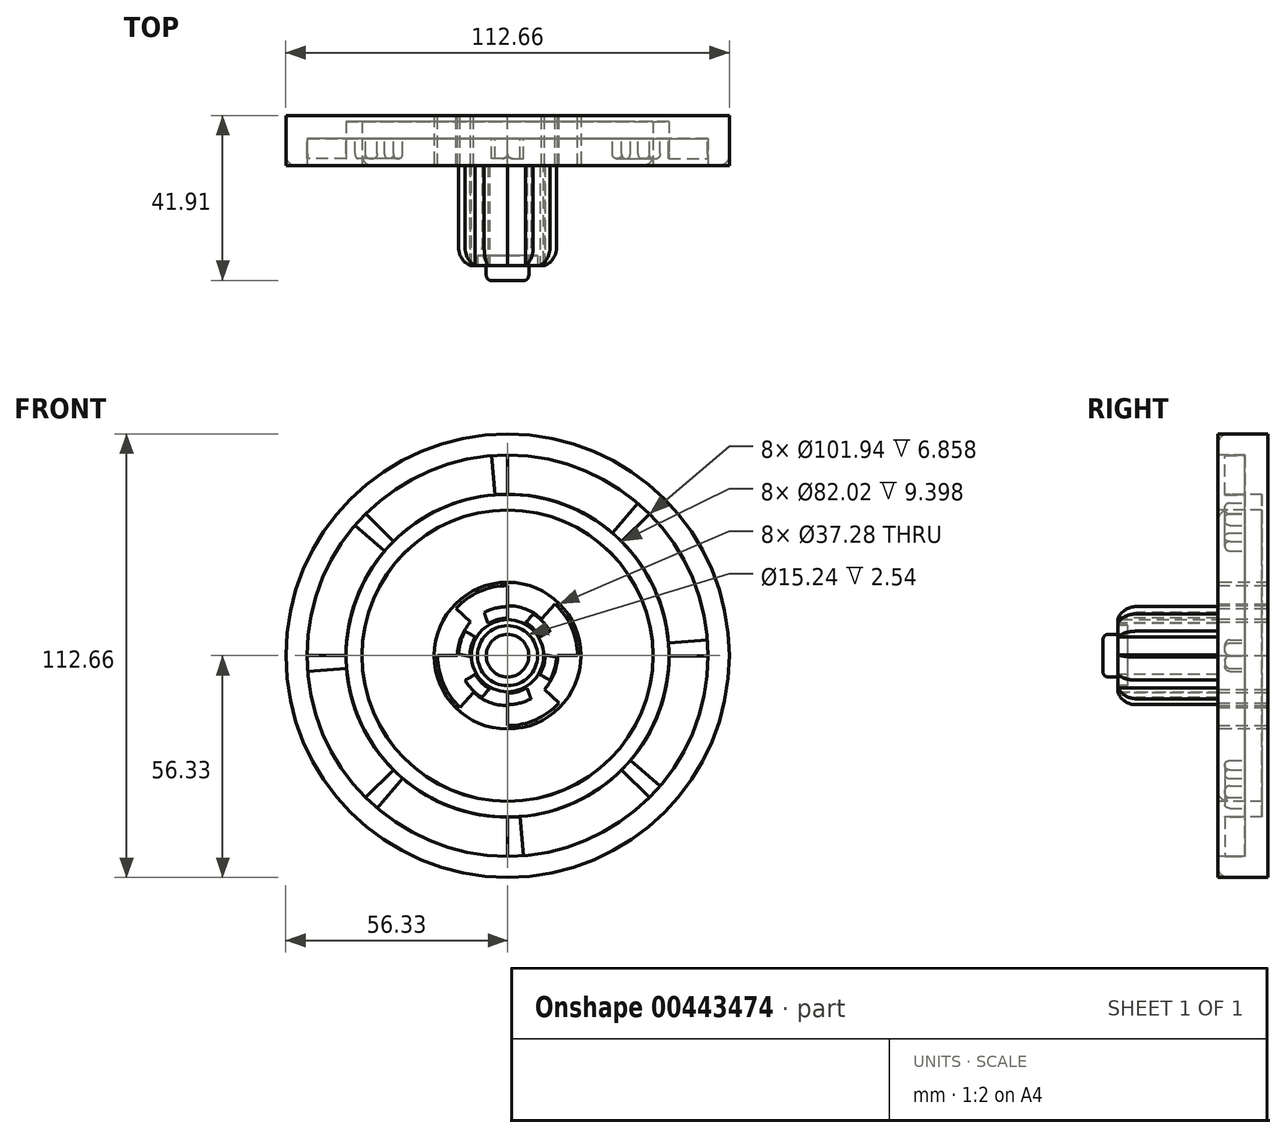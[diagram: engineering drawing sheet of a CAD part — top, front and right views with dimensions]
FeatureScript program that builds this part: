
annotation { "Feature Type Name" : "Feature", "Feature Type Description" : "" }
export const myFeature = defineFeature(function(context is Context, id is Id, definition is map)
    precondition{}
    {
        {
            var Q0;
            Q0=qCreatedBy(makeId("Front.planeOp"),FACE);
            var sketch = newSketch(context, id + "F0", { "sketchPlane" : qUnion([Q0])});
            skCircle(sketch, "E0", {"center": v(0, 0) * mm, "radius": 56.33 * mm});
            skSolve(sketch);
        }
        {
            var Q0;
            Q0=makeQuery(id+"F0.imprint","IMPRINT",FACE,{"disambiguationData":[TD([[makeQuery(id+"F0.imprint","IMPRINT",EDGE,{"derivedFrom":sQuery(id+"F0.wireOp",EDGE,"E0")}),1.0]])]});
            extrude(context, id + "F1", {"entities" : qUnion([Q0]), "depth" : 12.7 * mm});
        }
        {
            var Q0;
            Q0=makeQuery(id+"F1.opExtrude","CAP_FACE",FACE,{"disambiguationData":[OSD([sQuery(id+"F0.wireOp",EDGE,"E0")])],"isStart":false});
            var sketch = newSketch(context, id + "F2", { "sketchPlane" : qUnion([Q0])});
            skCircle(sketch, "E1", {"center": v(0, 0) * mm, "radius": 36.97 * mm});
            skCircle(sketch, "E2", {"center": v(0, 0) * mm, "radius": 50.97 * mm});
            skSolve(sketch);
        }
        {
            var Q0;
            Q0=makeQuery(id+"F2.imprint","IMPRINT",FACE,{"disambiguationData":[TD([[makeQuery(id+"F2.imprint","IMPRINT",EDGE,{"derivedFrom":sQuery(id+"F2.wireOp",EDGE,"E1")}),-1.0]])]});
            extrude(context, id + "F3", {"entities" : qUnion([Q0]), "operationType" : NewBodyOperationType.REMOVE, "oppositeDirection" : true, "depth" : 6.86 * mm});
        }
        {
            var Q0;
            Q0=makeQuery(id+"F3.boolean.opBoolean","COPY",FACE,{"derivedFrom":makeQuery(id+"F3.opExtrude","CAP_FACE",FACE,{"disambiguationData":[OSD([sQuery(id+"F2.wireOp",EDGE,"E1"),sQuery(id+"F2.wireOp",EDGE,"E2")])],"isStart":false})});
            var sketch = newSketch(context, id + "F4", { "sketchPlane" : qUnion([Q0])});
            skCircle(sketch, "E3", {"center": v(0, 0) * mm, "radius": 36.99 * mm});
            skCircle(sketch, "E4", {"center": v(0, 0) * mm, "radius": 41 * mm});
            skSolve(sketch);
        }
        {
            var Q0;
            Q0=makeQuery(id+"F4.imprint","IMPRINT",FACE,{"disambiguationData":[TD([[makeQuery(id+"F4.imprint","IMPRINT",EDGE,{"derivedFrom":sQuery(id+"F4.wireOp",EDGE,"E3")}),-1.0]])]});
            extrude(context, id + "F5", {"entities" : qUnion([Q0]), "operationType" : NewBodyOperationType.REMOVE, "oppositeDirection" : true, "depth" : 4.32 * mm});
        }
        {
            var Q0;
            {var subQ0=sQuery(id+"F2.wireOp",EDGE,"E2");Q0=makeQuery(id+"F5.boolean.opBoolean","SPLIT",FACE,{"disambiguationData":[TD([makeQuery(id+"F3.boolean.opBoolean","COPY",FACE,{"derivedFrom":makeQuery(id+"F3.opExtrude","SWEPT_FACE",FACE,{"disambiguationData":[OSD([subQ0])]})})])],"derivedFrom":makeQuery(id+"F3.boolean.opBoolean","COPY",FACE,{"derivedFrom":makeQuery(id+"F3.opExtrude","CAP_FACE",FACE,{"disambiguationData":[OSD([sQuery(id+"F2.wireOp",EDGE,"E1"),subQ0])],"isStart":false})})});}
            var sketch = newSketch(context, id + "F6", { "sketchPlane" : qUnion([Q0])});
            skLineSegment(sketch, "E5", {"start": v(0, 0) * mm, "end": v(33.1, 38.77) * mm});
            skLineSegment(sketch, "E6", {"start": v(0, 0) * mm, "end": v(36.07, 36.02) * mm});
            skSolve(sketch);
        }
        {
            var Q0;
            {var subQ0=sQuery(id+"F6.wireOp",EDGE,"E5");var subQ1=makeQuery(id+"F3.boolean.opBoolean","COPY",EDGE,{"derivedFrom":makeQuery(id+"F3.opExtrude","CAP_EDGE",EDGE,{"disambiguationData":[OSD([sQuery(id+"F2.wireOp",EDGE,"E2")])],"isStart":false})});var subQ2=makeQuery(id+"F6.imprint","INTERSECT",VERTEX,{"derivedFrom":[subQ1,subQ0]});Q0=makeQuery(id+"F6.imprint","IMPRINT",FACE,{"disambiguationData":[TD([[makeQuery(id+"F6.imprint","IMPRINT",EDGE,{"disambiguationData":[TD([[subQ2,1.0]])],"derivedFrom":subQ0}),-1.0]])]});}
            extrude(context, id + "F7", {"entities" : qUnion([Q0]), "operationType" : NewBodyOperationType.ADD, "depth" : 5.08 * mm});
        }
        {
            var Q0;
            Q0=makeQuery(id+"F7.opExtrude","CAP_EDGE",EDGE,{"disambiguationData":[OSD([sQuery(id+"F6.wireOp",EDGE,"E6")])],"isStart":false});
            fillet(context, id + "F8", {"entities" : qUnion([Q0]), "radius" : 1.27 * mm, "tangentPropagation" : true, "allowEdgeOverflow" : false});
        }
        {
            var Q0;
            Q0=makeQuery(id+"F1.opExtrude","SWEPT_BODY",BODY,{"disambiguationData":[OSD([sQuery(id+"F0.wireOp",EDGE,"E0")])]});
            var Q1;
            Q1=makeQuery(id+"F3.boolean.opBoolean","COPY",EDGE,{"derivedFrom":makeQuery(id+"F3.opExtrude","CAP_EDGE",EDGE,{"disambiguationData":[OSD([sQuery(id+"F2.wireOp",EDGE,"E1")])],"isStart":true})});
            circularPattern(context, id + "F9", {"entities" : qUnion([Q0]), "axis" : qUnion([Q1]), "angle" : 360 * degree, "instanceCount" : 8, "equalSpace" : true});
        }
        {
            var Q0;
            Q0=makeQuery(id+"F3.boolean.opBoolean","COPY",EDGE,{"derivedFrom":makeQuery(id+"F3.opExtrude","CAP_EDGE",EDGE,{"disambiguationData":[OSD([sQuery(id+"F2.wireOp",EDGE,"E1")])],"isStart":true})});
            fillet(context, id + "F10", {"entities" : qUnion([Q0]), "radius" : 2.54 * mm, "tangentPropagation" : true, "allowEdgeOverflow" : false});
        }
        {
            var Q0;
            Q0=makeQuery(id+"F3.boolean.opBoolean","COPY",EDGE,{"derivedFrom":makeQuery(id+"F3.opExtrude","CAP_EDGE",EDGE,{"disambiguationData":[OSD([sQuery(id+"F2.wireOp",EDGE,"E2")])],"isStart":true})});
            var Q1;
            Q1=makeQuery(id+"F1.opExtrude","CAP_EDGE",EDGE,{"disambiguationData":[OSD([sQuery(id+"F0.wireOp",EDGE,"E0")])],"isStart":false});
            var Q2;
            Q2=makeQuery(id+"F5.boolean.opBoolean","COPY",EDGE,{"derivedFrom":makeQuery(id+"F5.opExtrude","CAP_EDGE",EDGE,{"disambiguationData":[OSD([sQuery(id+"F4.wireOp",EDGE,"E4")])],"isStart":true})});
            fillet(context, id + "F11", {"entities" : qUnion([Q0, Q1, Q2]), "radius" : 2.54 * mm, "tangentPropagation" : true, "allowEdgeOverflow" : false});
        }
        {
            var Q0;
            Q0=makeQuery(id+"F9.opPattern","COPY",FACE,{"derivedFrom":makeQuery(id+"F3.boolean.opBoolean","SPLIT",FACE,{"disambiguationData":[TD([makeQuery(id+"F3.opExtrude","SWEPT_FACE",FACE,{"disambiguationData":[OSD([sQuery(id+"F2.wireOp",EDGE,"E1")])]})])],"derivedFrom":makeQuery(id+"F1.opExtrude","CAP_FACE",FACE,{"disambiguationData":[OSD([sQuery(id+"F0.wireOp",EDGE,"E0")])],"isStart":false})}),"instanceName":"5"});
            var sketch = newSketch(context, id + "F12", { "sketchPlane" : qUnion([Q0])});
            skCircle(sketch, "E7", {"center": v(0, 0) * mm, "radius": 18.64 * mm});
            skSolve(sketch);
        }
        {
            var Q0;
            Q0=makeQuery(id+"F12.imprint","IMPRINT",FACE,{"disambiguationData":[TD([[makeQuery(id+"F12.imprint","IMPRINT",EDGE,{"derivedFrom":sQuery(id+"F12.wireOp",EDGE,"E7")}),1.0]])]});
            extrude(context, id + "F13", {"entities" : qUnion([Q0]), "operationType" : NewBodyOperationType.REMOVE, "oppositeDirection" : true, "depth" : 25.4 * mm});
        }
        {
            var Q0;
            Q0=qCreatedBy(makeId("Front.planeOp"),FACE);
            var sketch = newSketch(context, id + "F14", { "sketchPlane" : qUnion([Q0])});
            skCircle(sketch, "E8", {"center": v(0, 0) * mm, "radius": 12.7 * mm});
            skCircle(sketch, "E9", {"center": v(0, 0) * mm, "radius": 17.78 * mm});
            skLineSegment(sketch, "E10", {"start": v(0, 0) * mm, "end": v(0, 17.78) * mm});
            skLineSegment(sketch, "E11", {"start": v(0, 0) * mm, "end": v(12, 13.12) * mm});
            skLineSegment(sketch, "E12", {"start": v(0, 0) * mm, "end": v(17.78, 0) * mm});
            skLineSegment(sketch, "E13", {"start": v(0, 0) * mm, "end": v(13.12, -12) * mm});
            skLineSegment(sketch, "E14", {"start": v(0, 0) * mm, "end": v(0, -17.78) * mm});
            skLineSegment(sketch, "E15", {"start": v(0, 0) * mm, "end": v(-12, -13.12) * mm});
            skLineSegment(sketch, "E16", {"start": v(0, 0) * mm, "end": v(-17.78, 0) * mm});
            skLineSegment(sketch, "E17", {"start": v(0, 0) * mm, "end": v(-13.12, 12) * mm});
            skSolve(sketch);
        }
        {
            var Q0;
            Q0=makeQuery(id+"F14.imprint","IMPRINT",FACE,{"disambiguationData":[TD([[makeQuery(id+"F14.imprint","IMPRINT",EDGE,{"derivedFrom":sQuery(id+"F14.wireOp",EDGE,"E8")}),1.0]])]});
            var Q1;
            {var subQ0=sQuery(id+"F14.wireOp",EDGE,"E11");var subQ1=sQuery(id+"F14.wireOp",EDGE,"E8");var subQ2=makeQuery(id+"F14.imprint","INTERSECT",VERTEX,{"derivedFrom":[subQ1,subQ0]});Q1=makeQuery(id+"F14.imprint","IMPRINT",FACE,{"disambiguationData":[TD([[makeQuery(id+"F14.imprint","IMPRINT",EDGE,{"disambiguationData":[TD([[subQ2,1.0]])],"derivedFrom":subQ1}),-1.0]])]});}
            var Q2;
            {var subQ0=sQuery(id+"F14.wireOp",EDGE,"E14");var subQ1=sQuery(id+"F14.wireOp",EDGE,"E8");var subQ2=makeQuery(id+"F14.imprint","INTERSECT",VERTEX,{"derivedFrom":[subQ1,subQ0]});Q2=makeQuery(id+"F14.imprint","IMPRINT",FACE,{"disambiguationData":[TD([[makeQuery(id+"F14.imprint","IMPRINT",EDGE,{"disambiguationData":[TD([[subQ2,-1.0]])],"derivedFrom":subQ1}),-1.0]])]});}
            var Q3;
            {var subQ0=sQuery(id+"F14.wireOp",EDGE,"E16");var subQ1=sQuery(id+"F14.wireOp",EDGE,"E8");var subQ2=makeQuery(id+"F14.imprint","INTERSECT",VERTEX,{"derivedFrom":[subQ1,subQ0]});Q3=makeQuery(id+"F14.imprint","IMPRINT",FACE,{"disambiguationData":[TD([[makeQuery(id+"F14.imprint","IMPRINT",EDGE,{"disambiguationData":[TD([[subQ2,-1.0]])],"derivedFrom":subQ1}),-1.0]])]});}
            var Q4;
            {var subQ0=sQuery(id+"F14.wireOp",EDGE,"E10");var subQ1=sQuery(id+"F14.wireOp",EDGE,"E8");var subQ2=makeQuery(id+"F14.imprint","INTERSECT",VERTEX,{"derivedFrom":[subQ1,subQ0]});Q4=makeQuery(id+"F14.imprint","IMPRINT",FACE,{"disambiguationData":[TD([[makeQuery(id+"F14.imprint","IMPRINT",EDGE,{"disambiguationData":[TD([[subQ2,-1.0]])],"derivedFrom":subQ1}),-1.0]])]});}
            extrude(context, id + "F15", {"entities" : qUnion([Q0, Q1, Q2, Q3, Q4]), "depth" : 12.7 * mm});
        }
        {
            var Q0;
            Q0=makeQuery(id+"F9.opPattern","COPY",EDGE,{"derivedFrom":makeQuery(id+"F7.opExtrude","CAP_EDGE",EDGE,{"disambiguationData":[OSD([sQuery(id+"F6.wireOp",EDGE,"E5")])],"isStart":false}),"instanceName":"2"});
            var Q1;
            Q1=makeQuery(id+"F9.opPattern","COPY",EDGE,{"derivedFrom":makeQuery(id+"F7.opExtrude","CAP_EDGE",EDGE,{"disambiguationData":[OSD([sQuery(id+"F6.wireOp",EDGE,"E5")])],"isStart":false}),"instanceName":"3"});
            var Q2;
            Q2=makeQuery(id+"F7.opExtrude","CAP_EDGE",EDGE,{"disambiguationData":[OSD([sQuery(id+"F6.wireOp",EDGE,"E5")])],"isStart":false});
            var Q3;
            Q3=makeQuery(id+"F9.opPattern","COPY",EDGE,{"derivedFrom":makeQuery(id+"F7.opExtrude","CAP_EDGE",EDGE,{"disambiguationData":[OSD([sQuery(id+"F6.wireOp",EDGE,"E5")])],"isStart":false}),"instanceName":"7"});
            var Q4;
            Q4=makeQuery(id+"F9.opPattern","COPY",EDGE,{"derivedFrom":makeQuery(id+"F7.opExtrude","CAP_EDGE",EDGE,{"disambiguationData":[OSD([sQuery(id+"F6.wireOp",EDGE,"E5")])],"isStart":false}),"instanceName":"6"});
            var Q5;
            Q5=makeQuery(id+"F9.opPattern","COPY",EDGE,{"derivedFrom":makeQuery(id+"F7.opExtrude","CAP_EDGE",EDGE,{"disambiguationData":[OSD([sQuery(id+"F6.wireOp",EDGE,"E5")])],"isStart":false}),"instanceName":"4"});
            fillet(context, id + "F16", {"entities" : qUnion([Q0, Q1, Q2, Q3, Q4, Q5]), "radius" : 1.27 * mm, "tangentPropagation" : true, "allowEdgeOverflow" : false});
        }
        {
            var Q0;
            Q0=makeQuery(id+"F15.opExtrude","CAP_FACE",FACE,{"disambiguationData":[OSD([sQuery(id+"F14.wireOp",EDGE,"E8"),sQuery(id+"F14.wireOp",EDGE,"E9"),sQuery(id+"F14.wireOp",EDGE,"E10"),sQuery(id+"F14.wireOp",EDGE,"E11"),sQuery(id+"F14.wireOp",EDGE,"E12"),sQuery(id+"F14.wireOp",EDGE,"E13"),sQuery(id+"F14.wireOp",EDGE,"E14"),sQuery(id+"F14.wireOp",EDGE,"E15"),sQuery(id+"F14.wireOp",EDGE,"E16"),sQuery(id+"F14.wireOp",EDGE,"E17")])],"isStart":false});
            var sketch = newSketch(context, id + "F17", { "sketchPlane" : qUnion([Q0])});
            skCircle(sketch, "E18", {"center": v(0, 0) * mm, "radius": 9.16 * mm});
            skSolve(sketch);
        }
        {
            var Q0;
            Q0=makeQuery(id+"F17.imprint","IMPRINT",FACE,{"disambiguationData":[TD([[makeQuery(id+"F17.imprint","IMPRINT",EDGE,{"derivedFrom":sQuery(id+"F17.wireOp",EDGE,"E18")}),1.0]])]});
            var sketch = newSketch(context, id + "F18", { "sketchPlane" : qUnion([Q0])});
            skCircle(sketch, "E19", {"center": v(0, 0) * mm, "radius": 9.53 * mm});
            skCircle(sketch, "E20", {"center": v(0, 0) * mm, "radius": 12.45 * mm});
            skLineSegment(sketch, "E21", {"start": v(-4.26, 8.52) * mm, "end": v(-5.57, 11.13) * mm});
            skLineSegment(sketch, "E22", {"start": v(0, 9.53) * mm, "end": v(0, 12.45) * mm});
            skLineSegment(sketch, "E23", {"start": v(4.44, 8.43) * mm, "end": v(5.8, 11.01) * mm});
            skLineSegment(sketch, "E24", {"start": v(8.52, 4.26) * mm, "end": v(11.13, 5.57) * mm});
            skLineSegment(sketch, "E25", {"start": v(9.53, 0) * mm, "end": v(12.45, 0) * mm});
            skLineSegment(sketch, "E26", {"start": v(8.43, -4.44) * mm, "end": v(11.01, -5.8) * mm});
            skLineSegment(sketch, "E27", {"start": v(4.26, -8.52) * mm, "end": v(5.57, -11.13) * mm});
            skLineSegment(sketch, "E28", {"start": v(0, -9.53) * mm, "end": v(0, -12.45) * mm});
            skLineSegment(sketch, "E29", {"start": v(-4.44, -8.43) * mm, "end": v(-5.8, -11.01) * mm});
            skLineSegment(sketch, "E30", {"start": v(-8.52, -4.26) * mm, "end": v(-11.13, -5.57) * mm});
            skLineSegment(sketch, "E31", {"start": v(-9.53, 0) * mm, "end": v(-12.45, 0) * mm});
            skLineSegment(sketch, "E32", {"start": v(-8.43, 4.44) * mm, "end": v(-11.01, 5.8) * mm});
            skSolve(sketch);
        }
        {
            var Q0;
            Q0=makeQuery(id+"F17.imprint","IMPRINT",FACE,{"disambiguationData":[TD([[makeQuery(id+"F17.imprint","IMPRINT",EDGE,{"derivedFrom":sQuery(id+"F17.wireOp",EDGE,"E18")}),1.0]])]});
            var Q1;
            Q1 = qSketchRegion(id + "F18", true);
            extrude(context, id + "F19", {"entities" : qUnion([Q0, Q1]), "depth" : 25.4 * mm});
        }
        {
            var Q0;
            Q0=makeQuery(id+"F19.opExtrude","CAP_FACE",FACE,{"disambiguationData":[OSD([sQuery(id+"F18.wireOp",EDGE,"E19"),sQuery(id+"F18.wireOp",EDGE,"E20")])],"isStart":false});
            var sketch = newSketch(context, id + "F20", { "sketchPlane" : qUnion([Q0])});
            skLineSegment(sketch, "E33", {"start": v(0, 12.45) * mm, "end": v(0, 9.53) * mm});
            skLineSegment(sketch, "E34", {"start": v(4.6, 8.34) * mm, "end": v(6.52, 10.6) * mm});
            skArc(sketch, "E35", {"start": v(0, 12.45) * mm, "mid": v(3.39, 11.98) * mm, "end": v(6.52, 10.6) * mm});
            skArc(sketch, "E36", {"start": v(0, 9.53) * mm, "mid": v(2.37, 9.22) * mm, "end": v(4.6, 8.34) * mm});
            skLineSegment(sketch, "E37.1.0", {"start": v(-10.78, 6.22) * mm, "end": v(-8.25, 4.76) * mm});
            skArc(sketch, "E37.1.1", {"start": v(-10.78, 6.22) * mm, "mid": v(-8.68, 8.92) * mm, "end": v(-5.92, 10.95) * mm});
            skLineSegment(sketch, "E37.1.2", {"start": v(-4.93, 8.15) * mm, "end": v(-5.92, 10.95) * mm});
            skArc(sketch, "E37.1.3", {"start": v(-8.25, 4.76) * mm, "mid": v(-6.8, 6.67) * mm, "end": v(-4.93, 8.15) * mm});
            skLineSegment(sketch, "E37.2.0", {"start": v(-10.78, -6.22) * mm, "end": v(-8.25, -4.76) * mm});
            skArc(sketch, "E37.2.1", {"start": v(-10.78, -6.22) * mm, "mid": v(-12.07, -3.06) * mm, "end": v(-12.44, 0.34) * mm});
            skLineSegment(sketch, "E37.2.2", {"start": v(-9.52, -0.2) * mm, "end": v(-12.44, 0.34) * mm});
            skArc(sketch, "E37.2.3", {"start": v(-8.25, -4.76) * mm, "mid": v(-9.18, -2.56) * mm, "end": v(-9.52, -0.2) * mm});
            skLineSegment(sketch, "E37.3.0", {"start": v(0, -12.45) * mm, "end": v(0, -9.53) * mm});
            skArc(sketch, "E37.3.1", {"start": v(0, -12.45) * mm, "mid": v(-3.39, -11.98) * mm, "end": v(-6.52, -10.6) * mm});
            skLineSegment(sketch, "E37.3.2", {"start": v(-4.6, -8.34) * mm, "end": v(-6.52, -10.6) * mm});
            skArc(sketch, "E37.3.3", {"start": v(0, -9.53) * mm, "mid": v(-2.37, -9.22) * mm, "end": v(-4.6, -8.34) * mm});
            skLineSegment(sketch, "E37.4.0", {"start": v(10.78, -6.22) * mm, "end": v(8.25, -4.76) * mm});
            skArc(sketch, "E37.4.1", {"start": v(10.78, -6.22) * mm, "mid": v(8.68, -8.92) * mm, "end": v(5.92, -10.95) * mm});
            skLineSegment(sketch, "E37.4.2", {"start": v(4.93, -8.15) * mm, "end": v(5.92, -10.95) * mm});
            skArc(sketch, "E37.4.3", {"start": v(8.25, -4.76) * mm, "mid": v(6.8, -6.67) * mm, "end": v(4.93, -8.15) * mm});
            skLineSegment(sketch, "E37.5.0", {"start": v(10.78, 6.22) * mm, "end": v(8.25, 4.76) * mm});
            skArc(sketch, "E37.5.1", {"start": v(10.78, 6.22) * mm, "mid": v(12.07, 3.06) * mm, "end": v(12.44, -0.34) * mm});
            skLineSegment(sketch, "E37.5.2", {"start": v(9.52, 0.2) * mm, "end": v(12.44, -0.34) * mm});
            skArc(sketch, "E37.5.3", {"start": v(8.25, 4.76) * mm, "mid": v(9.18, 2.56) * mm, "end": v(9.52, 0.2) * mm});
            skSolve(sketch);
        }
        {
            var Q0;
            Q0=makeQuery(id+"F20.imprint","IMPRINT",FACE,{"disambiguationData":[TD([[makeQuery(id+"F20.imprint","IMPRINT",EDGE,{"derivedFrom":sQuery(id+"F20.wireOp",EDGE,"E33")}),1.0]])]});
            var Q1;
            Q1=makeQuery(id+"F20.imprint","IMPRINT",FACE,{"disambiguationData":[TD([[makeQuery(id+"F20.imprint","IMPRINT",EDGE,{"derivedFrom":sQuery(id+"F20.wireOp",EDGE,"E37.5.0")}),1.0]])]});
            var Q2;
            Q2=makeQuery(id+"F20.imprint","IMPRINT",FACE,{"disambiguationData":[TD([[makeQuery(id+"F20.imprint","IMPRINT",EDGE,{"derivedFrom":sQuery(id+"F20.wireOp",EDGE,"E37.4.0")}),1.0]])]});
            var Q3;
            Q3=makeQuery(id+"F20.imprint","IMPRINT",FACE,{"disambiguationData":[TD([[makeQuery(id+"F20.imprint","IMPRINT",EDGE,{"derivedFrom":sQuery(id+"F20.wireOp",EDGE,"E37.3.0")}),1.0]])]});
            var Q4;
            Q4=makeQuery(id+"F20.imprint","IMPRINT",FACE,{"disambiguationData":[TD([[makeQuery(id+"F20.imprint","IMPRINT",EDGE,{"derivedFrom":sQuery(id+"F20.wireOp",EDGE,"E37.2.0")}),1.0]])]});
            var Q5;
            Q5=makeQuery(id+"F20.imprint","IMPRINT",FACE,{"disambiguationData":[TD([[makeQuery(id+"F20.imprint","IMPRINT",EDGE,{"derivedFrom":sQuery(id+"F20.wireOp",EDGE,"E37.1.0")}),1.0]])]});
            extrude(context, id + "F21", {"entities" : qUnion([Q0, Q1, Q2, Q3, Q4, Q5]), "operationType" : NewBodyOperationType.REMOVE, "oppositeDirection" : true, "depth" : 25.4 * mm});
        }
        {
            var Q0;
            {var subQ0=sQuery(id+"F18.wireOp",EDGE,"E20");Q0=makeQuery(id+"F21.boolean.opBoolean","SPLIT",EDGE,{"disambiguationData":[TD([makeQuery(id+"F21.opExtrude","SWEPT_FACE",FACE,{"disambiguationData":[OSD([sQuery(id+"F20.wireOp",EDGE,"E34")])]})])],"derivedFrom":makeQuery(id+"F19.opExtrude","CAP_EDGE",EDGE,{"disambiguationData":[OSD([subQ0])],"isStart":false})});}
            var Q1;
            {var subQ0=sQuery(id+"F18.wireOp",EDGE,"E20");Q1=makeQuery(id+"F21.boolean.opBoolean","SPLIT",EDGE,{"disambiguationData":[TD([makeQuery(id+"F21.opExtrude","SWEPT_FACE",FACE,{"disambiguationData":[OSD([sQuery(id+"F20.wireOp",EDGE,"E33")])]})])],"derivedFrom":makeQuery(id+"F19.opExtrude","CAP_EDGE",EDGE,{"disambiguationData":[OSD([subQ0])],"isStart":false})});}
            var Q2;
            {var subQ0=sQuery(id+"F18.wireOp",EDGE,"E20");Q2=makeQuery(id+"F21.boolean.opBoolean","SPLIT",EDGE,{"disambiguationData":[TD([makeQuery(id+"F21.opExtrude","SWEPT_FACE",FACE,{"disambiguationData":[OSD([sQuery(id+"F20.wireOp",EDGE,"E37.1.0")])]})])],"derivedFrom":makeQuery(id+"F19.opExtrude","CAP_EDGE",EDGE,{"disambiguationData":[OSD([subQ0])],"isStart":false})});}
            var Q3;
            {var subQ0=sQuery(id+"F18.wireOp",EDGE,"E20");Q3=makeQuery(id+"F21.boolean.opBoolean","SPLIT",EDGE,{"disambiguationData":[TD([makeQuery(id+"F21.opExtrude","SWEPT_FACE",FACE,{"disambiguationData":[OSD([sQuery(id+"F20.wireOp",EDGE,"E37.2.0")])]})])],"derivedFrom":makeQuery(id+"F19.opExtrude","CAP_EDGE",EDGE,{"disambiguationData":[OSD([subQ0])],"isStart":false})});}
            var Q4;
            {var subQ0=sQuery(id+"F18.wireOp",EDGE,"E20");Q4=makeQuery(id+"F21.boolean.opBoolean","SPLIT",EDGE,{"disambiguationData":[TD([makeQuery(id+"F21.opExtrude","SWEPT_FACE",FACE,{"disambiguationData":[OSD([sQuery(id+"F20.wireOp",EDGE,"E37.3.0")])]})])],"derivedFrom":makeQuery(id+"F19.opExtrude","CAP_EDGE",EDGE,{"disambiguationData":[OSD([subQ0])],"isStart":false})});}
            var Q5;
            {var subQ0=sQuery(id+"F18.wireOp",EDGE,"E20");Q5=makeQuery(id+"F21.boolean.opBoolean","SPLIT",EDGE,{"disambiguationData":[TD([makeQuery(id+"F21.opExtrude","SWEPT_FACE",FACE,{"disambiguationData":[OSD([sQuery(id+"F20.wireOp",EDGE,"E37.4.0")])]})])],"derivedFrom":makeQuery(id+"F19.opExtrude","CAP_EDGE",EDGE,{"disambiguationData":[OSD([subQ0])],"isStart":false})});}
            fillet(context, id + "F22", {"entities" : qUnion([Q0, Q1, Q2, Q3, Q4, Q5]), "radius" : 5.08 * mm, "tangentPropagation" : true, "allowEdgeOverflow" : false});
        }
        {
            var Q0;
            Q0=makeQuery(id+"F19.opExtrude","CAP_FACE",FACE,{"disambiguationData":[OSD([sQuery(id+"F17.wireOp",EDGE,"E18")])],"isStart":false});
            var sketch = newSketch(context, id + "F23", { "sketchPlane" : qUnion([Q0])});
            skCircle(sketch, "E38", {"center": v(0, 0) * mm, "radius": 7.62 * mm});
            skSolve(sketch);
        }
        {
            var Q0;
            Q0=makeQuery(id+"F23.imprint","IMPRINT",FACE,{"disambiguationData":[TD([[makeQuery(id+"F23.imprint","IMPRINT",EDGE,{"derivedFrom":sQuery(id+"F23.wireOp",EDGE,"E38")}),1.0]])]});
            extrude(context, id + "F24", {"entities" : qUnion([Q0]), "operationType" : NewBodyOperationType.REMOVE, "oppositeDirection" : true, "depth" : 2.54 * mm});
        }
        {
            var Q0;
            Q0=makeQuery(id+"F24.boolean.opBoolean","COPY",FACE,{"derivedFrom":makeQuery(id+"F24.opExtrude","CAP_FACE",FACE,{"disambiguationData":[OSD([sQuery(id+"F23.wireOp",EDGE,"E38")])],"isStart":false})});
            var sketch = newSketch(context, id + "F25", { "sketchPlane" : qUnion([Q0])});
            skCircle(sketch, "E39", {"center": v(0, 0) * mm, "radius": 5.4 * mm});
            skSolve(sketch);
        }
        {
            var Q0;
            Q0=makeQuery(id+"F25.imprint","IMPRINT",FACE,{"disambiguationData":[TD([[makeQuery(id+"F25.imprint","IMPRINT",EDGE,{"derivedFrom":sQuery(id+"F25.wireOp",EDGE,"E39")}),1.0]])]});
            extrude(context, id + "F26", {"entities" : qUnion([Q0]), "operationType" : NewBodyOperationType.ADD, "depth" : 6.35 * mm});
        }
        {
            var Q0;
            Q0=makeQuery(id+"F26.opExtrude","CAP_EDGE",EDGE,{"disambiguationData":[OSD([sQuery(id+"F25.wireOp",EDGE,"E39")])],"isStart":false});
            fillet(context, id + "F27", {"entities" : qUnion([Q0]), "radius" : 1.27 * mm, "tangentPropagation" : true, "allowEdgeOverflow" : false});
        }
    });
